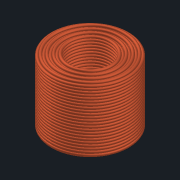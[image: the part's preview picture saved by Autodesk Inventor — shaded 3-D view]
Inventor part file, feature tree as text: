
AUTODESK INVENTOR PART (.ipt)
format: ipt  version: 2022.2 (Build 262287010, 287A)  size: 1,667,584 bytes
history: native  units: mm
features: revolve x1, sketch x1
ambient origin geometry x8: Origin, YZ Plane, XZ Plane, XY Plane, X Axis, Y Axis, Z Axis, Center Point
bodies: Solid1 (feature_tree)
feature tree (2):
  revolve  "Revolution1"  [1 undecoded]
  sketch  "Sketch2"  dims[d7=8.0mm d8=16.0mm d9=13.2mm d10=0.55mm d11=40.0mm d13=0.9527mm d14=10.0mm d16=10.0mm d18=90.0deg]
note: 1 required parameter value undecoded (feature->parameter linkage not recoverable at this tier; creation-order binding heuristic only, values carry confidence <= 0.55)
